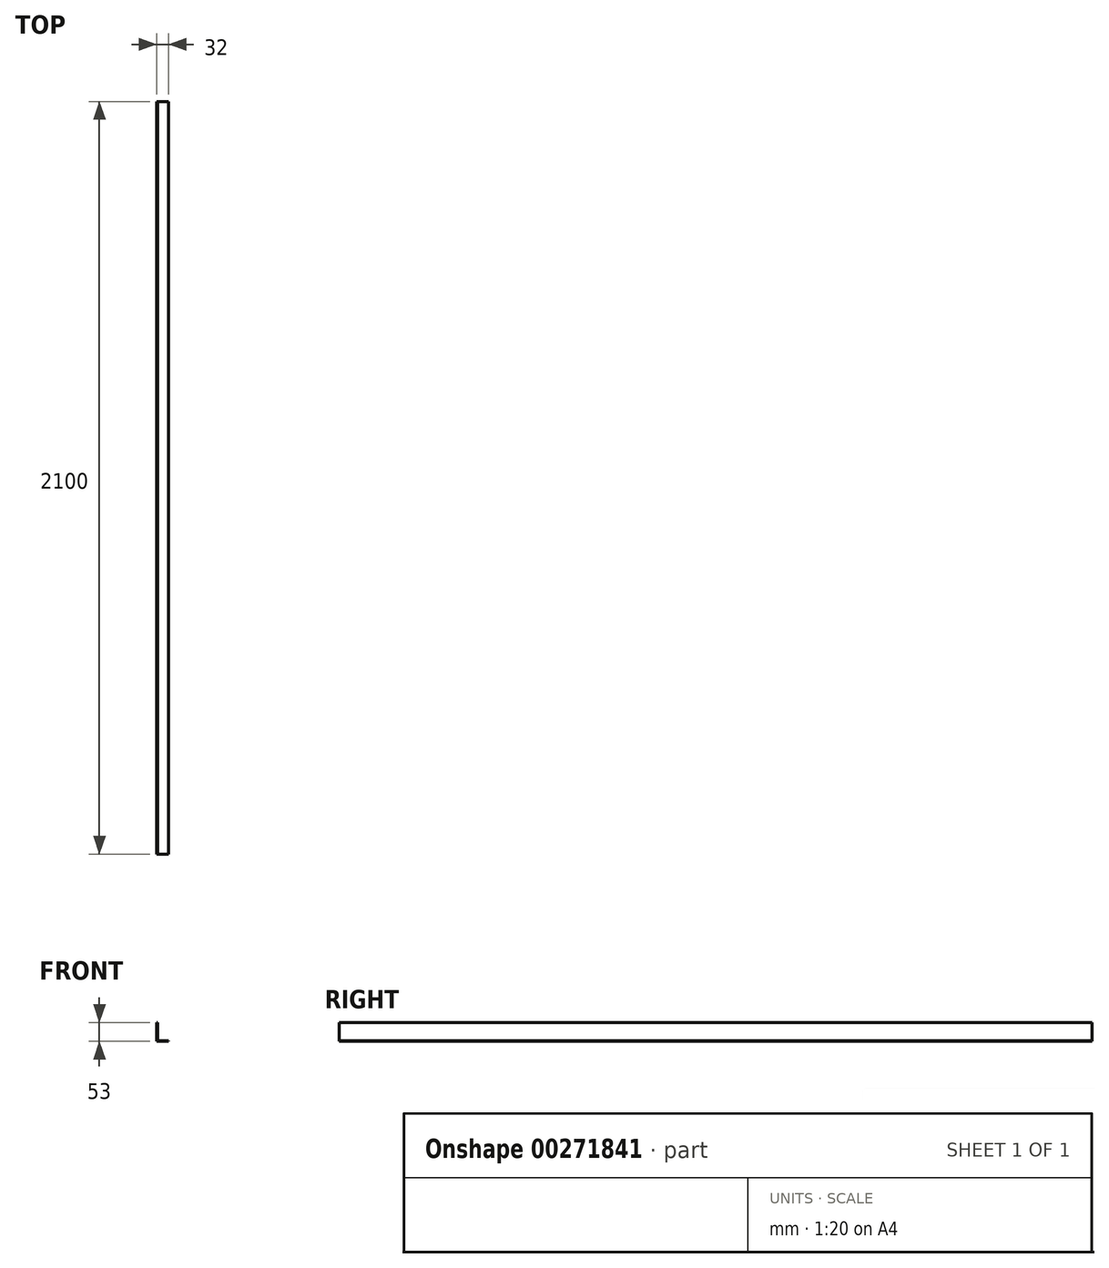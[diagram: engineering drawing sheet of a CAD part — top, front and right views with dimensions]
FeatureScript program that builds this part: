
annotation { "Feature Type Name" : "Feature", "Feature Type Description" : "" }
export const myFeature = defineFeature(function(context is Context, id is Id, definition is map)
    precondition{}
    {
        {
            var Q0;
            Q0=qCreatedBy(makeId("Front.planeOp"),FACE);
            var sketch = newSketch(context, id + "F0", { "sketchPlane" : qUnion([Q0])});
            skLineSegment(sketch, "E0", {"start": v(-39.5, 30.57) * mm, "end": v(-39.5, -22.43) * mm});
            skLineSegment(sketch, "E1", {"start": v(-39.5, -22.43) * mm, "end": v(-7.5, -22.43) * mm});
            skLineSegment(sketch, "E2", {"start": v(-7.5, -22.43) * mm, "end": v(-7.5, -20.23) * mm});
            skLineSegment(sketch, "E3", {"start": v(-7.5, -20.23) * mm, "end": v(-37.3, -20.23) * mm});
            skLineSegment(sketch, "E4", {"start": v(-37.3, -20.23) * mm, "end": v(-37.3, 30.57) * mm});
            skLineSegment(sketch, "E5", {"start": v(-37.3, 30.57) * mm, "end": v(-39.5, 30.57) * mm});
            skSolve(sketch);
        }
        {
            var Q0;
            Q0 = qSketchRegion(id + "F0", true);
            extrude(context, id + "F1", {"entities" : qUnion([Q0]), "depth" : 2100 * mm});
        }
    });
